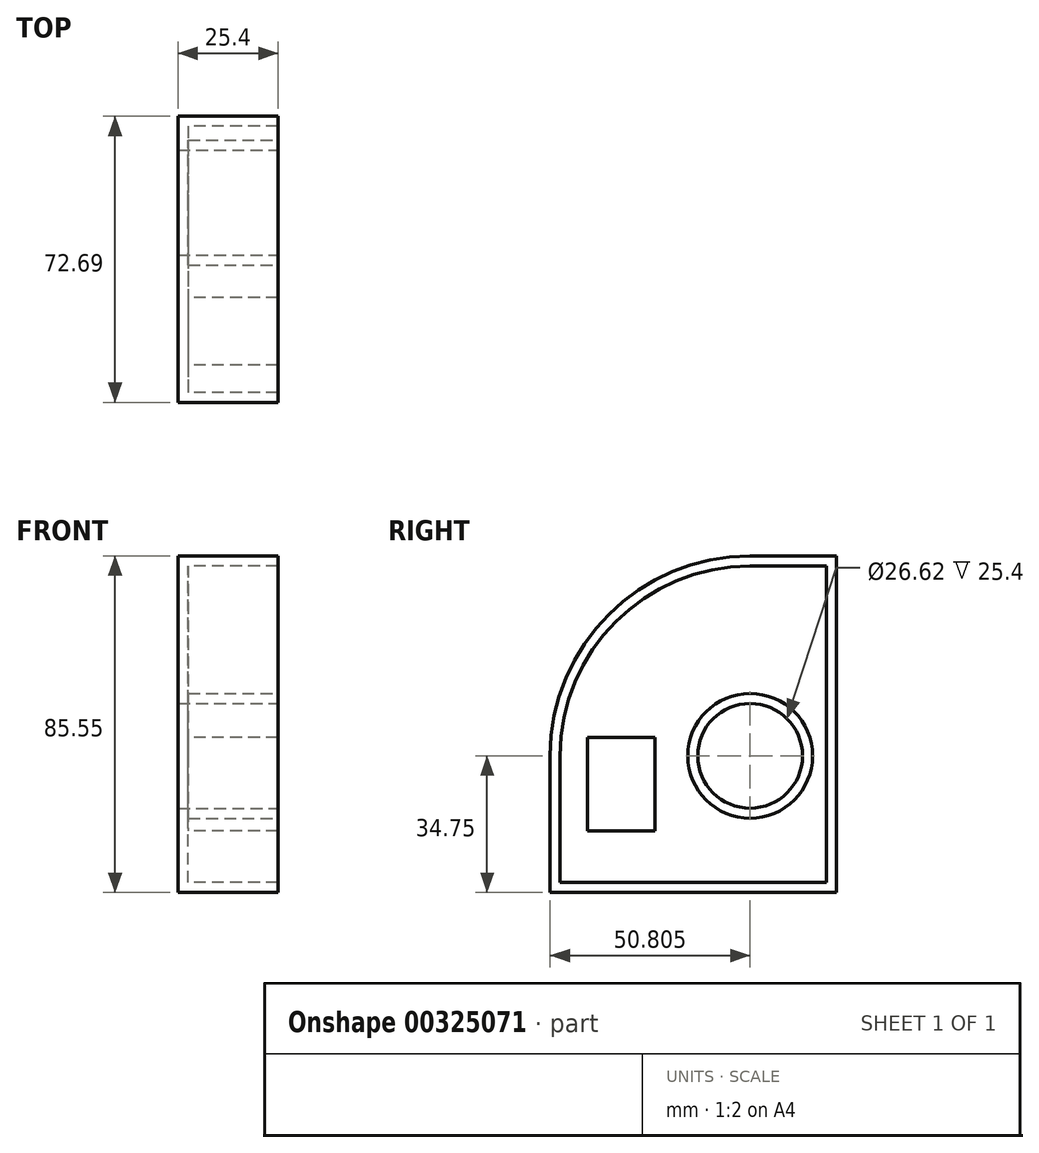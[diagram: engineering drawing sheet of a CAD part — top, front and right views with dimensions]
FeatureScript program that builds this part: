
annotation { "Feature Type Name" : "Feature", "Feature Type Description" : "" }
export const myFeature = defineFeature(function(context is Context, id is Id, definition is map)
    precondition{}
    {
        {
            var Q0;
            Q0=qCreatedBy(makeId("Right.planeOp"),FACE);
            var sketch = newSketch(context, id + "F0", { "sketchPlane" : qUnion([Q0])});
            skLineSegment(sketch, "E0.bottom", {"start": v(51.9, -55.34) * mm, "end": v(-20.8, -55.34) * mm});
            skLineSegment(sketch, "E0.top", {"start": v(51.9, 30.21) * mm, "end": v(-20.8, 30.21) * mm});
            skLineSegment(sketch, "E0.left", {"start": v(51.9, -55.34) * mm, "end": v(51.9, 30.21) * mm});
            skLineSegment(sketch, "E0.right", {"start": v(-20.8, -55.34) * mm, "end": v(-20.8, 30.21) * mm});
            skSolve(sketch);
        }
        {
            var Q0;
            Q0=makeQuery(id+"F0.imprint","IMPRINT",FACE,{"disambiguationData":[TD([[makeQuery(id+"F0.imprint","IMPRINT",EDGE,{"derivedFrom":sQuery(id+"F0.wireOp",EDGE,"E0.bottom")}),-1.0]])]});
            extrude(context, id + "F1", {"entities" : qUnion([Q0]), "depth" : 25.4 * mm});
        }
        {
            var Q0;
            Q0=makeQuery(id+"F1.opExtrude","SWEPT_EDGE",EDGE,{"disambiguationData":[OSD([sQuery(id+"F0.wireOp",EDGE,"E0.top"),sQuery(id+"F0.wireOp",EDGE,"E0.right")])]});
            fillet(context, id + "F2", {"entities" : qUnion([Q0]), "radius" : 50.8 * mm, "tangentPropagation" : true, "allowEdgeOverflow" : false});
        }
        {
            var Q0;
            Q0=makeQuery(id+"F1.opExtrude","CAP_FACE",FACE,{"disambiguationData":[OSD([sQuery(id+"F0.wireOp",EDGE,"E0.bottom"),sQuery(id+"F0.wireOp",EDGE,"E0.top"),sQuery(id+"F0.wireOp",EDGE,"E0.left"),sQuery(id+"F0.wireOp",EDGE,"E0.right")])],"isStart":false});
            var sketch = newSketch(context, id + "F3", { "sketchPlane" : qUnion([Q0])});
            skCircle(sketch, "E1", {"center": v(30, -20.59) * mm, "radius": 13.31 * mm});
            skSolve(sketch);
        }
        {
            var Q0;
            Q0=makeQuery(id+"F3.imprint","IMPRINT",FACE,{"disambiguationData":[TD([[makeQuery(id+"F3.imprint","IMPRINT",EDGE,{"derivedFrom":sQuery(id+"F3.wireOp",EDGE,"E1")}),1.0]])]});
            extrude(context, id + "F4", {"entities" : qUnion([Q0]), "operationType" : NewBodyOperationType.REMOVE, "oppositeDirection" : true, "depth" : 25.4 * mm});
        }
        {
            var Q0;
            Q0=makeQuery(id+"F1.opExtrude","CAP_FACE",FACE,{"disambiguationData":[OSD([sQuery(id+"F0.wireOp",EDGE,"E0.bottom"),sQuery(id+"F0.wireOp",EDGE,"E0.top"),sQuery(id+"F0.wireOp",EDGE,"E0.left"),sQuery(id+"F0.wireOp",EDGE,"E0.right")])],"isStart":false});
            shell(context, id + "F5", {"entities" : qUnion([Q0]), "thickness" : 2.54 * mm});
        }
        {
            var Q0;
            Q0=qCreatedBy(makeId("Right.planeOp"),FACE);
            var sketch = newSketch(context, id + "F6", { "sketchPlane" : qUnion([Q0])});
            skLineSegment(sketch, "E2.bottom", {"start": v(-11.3, -39.67) * mm, "end": v(5.8, -39.67) * mm});
            skLineSegment(sketch, "E2.top", {"start": v(-11.3, -15.92) * mm, "end": v(5.8, -15.92) * mm});
            skLineSegment(sketch, "E2.left", {"start": v(-11.3, -39.67) * mm, "end": v(-11.3, -15.92) * mm});
            skLineSegment(sketch, "E2.right", {"start": v(5.8, -39.67) * mm, "end": v(5.8, -15.92) * mm});
            skSolve(sketch);
        }
        {
            var Q0;
            Q0=makeQuery(id+"F6.imprint","IMPRINT",FACE,{"disambiguationData":[TD([[makeQuery(id+"F6.imprint","IMPRINT",EDGE,{"derivedFrom":sQuery(id+"F6.wireOp",EDGE,"E2.bottom")}),1.0]])]});
            extrude(context, id + "F7", {"entities" : qUnion([Q0]), "operationType" : NewBodyOperationType.ADD, "depth" : 25.4 * mm});
        }
    });
